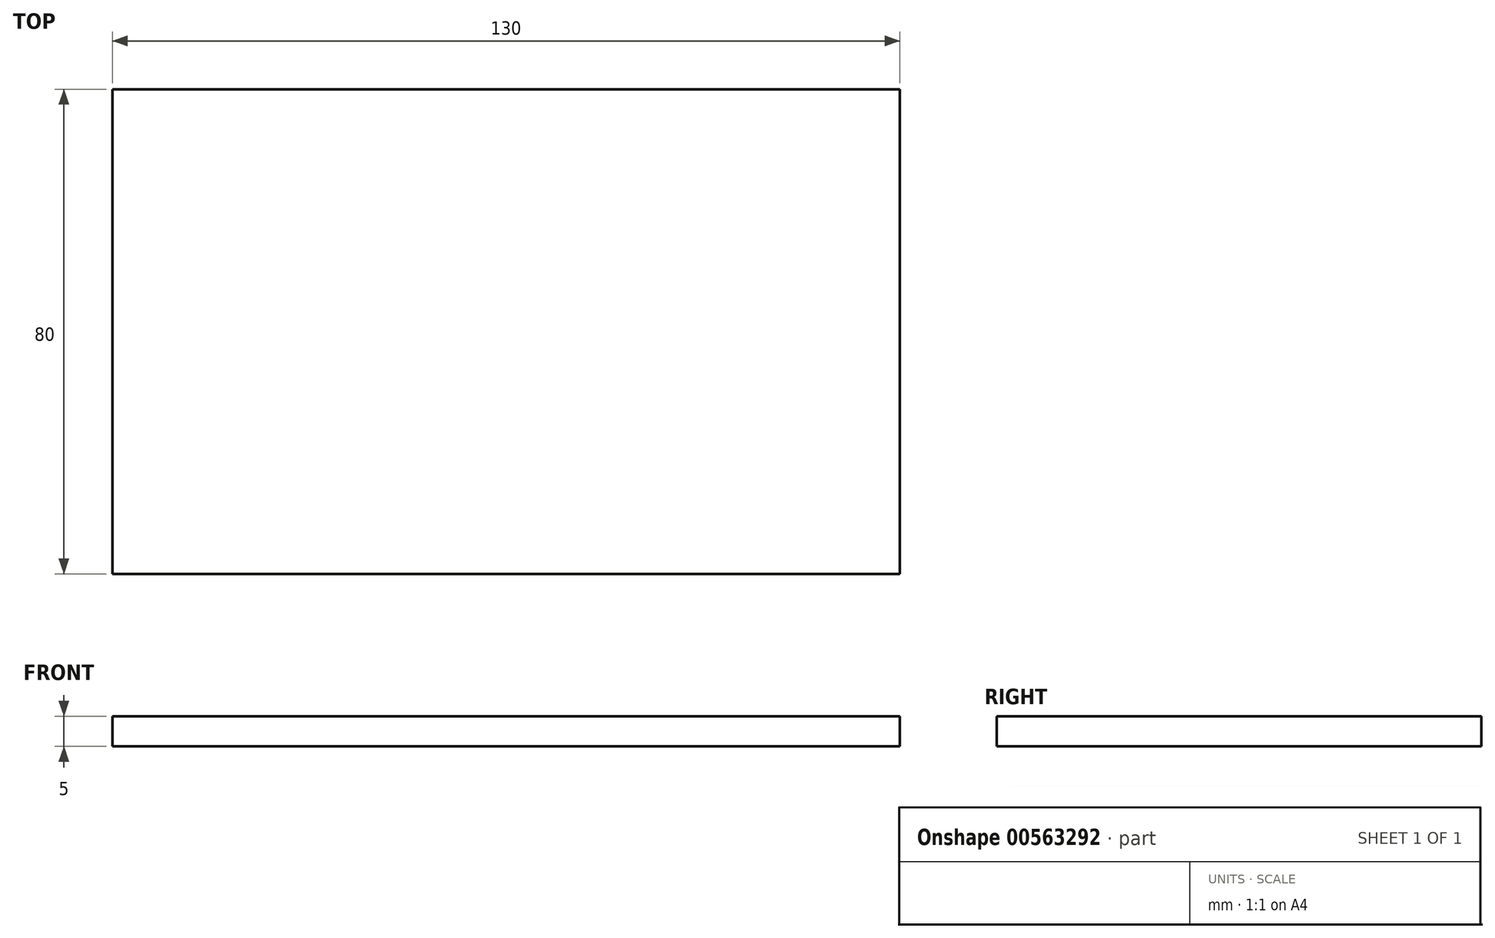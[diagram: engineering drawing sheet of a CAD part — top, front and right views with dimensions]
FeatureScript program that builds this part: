
annotation { "Feature Type Name" : "Feature", "Feature Type Description" : "" }
export const myFeature = defineFeature(function(context is Context, id is Id, definition is map)
    precondition{}
    {
        {
            var Q0;
            Q0=qCreatedBy(makeId("Top.planeOp"),FACE);
            var sketch = newSketch(context, id + "F0", { "sketchPlane" : qUnion([Q0])});
            skLineSegment(sketch, "E0.left", {"start": v(47.99, -27) * mm, "end": v(47.99, -107) * mm});
            skLineSegment(sketch, "E0.right", {"start": v(177.99, -27) * mm, "end": v(177.99, -107) * mm});
            skPoint(sketch, "E1.end.orphan", {"position": v(141.94, -107) * mm});
            skLineSegment(sketch, "E2", {"start": v(47.99, -27) * mm, "end": v(177.99, -27) * mm});
            skLineSegment(sketch, "E3", {"start": v(47.99, -107) * mm, "end": v(177.99, -107) * mm});
            skSolve(sketch);
        }
        {
            var Q0;
            Q0 = qSketchRegion(id + "F0", true);
            var Q1;
            Q1 = qConstructionFilter(qBodyType(qCreatedBy(id + "F0" ,EDGE), BodyType.WIRE), ConstructionObject.NO);
            extrude(context, id + "F1", {"entities" : qUnion([Q0]), "surfaceEntities" : qUnion([Q1]), "depth" : 5 * mm, "offsetDistance" : 25 * mm});
        }
    });
